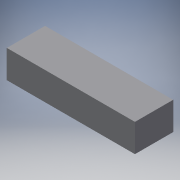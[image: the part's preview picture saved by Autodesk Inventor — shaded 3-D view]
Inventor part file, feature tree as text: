
AUTODESK INVENTOR PART (.ipt)
format: ipt  version: 2016 (Build 200138000, 138)  size: 91,648 bytes
history: native  units: mm
features: other x1, extrude x1, sketch x1
ambient origin geometry x8: Origin, YZ Plane, XZ Plane, XY Plane, X Axis, Y Axis, Z Axis, Center Point
bodies: Solid1 (feature_tree)
feature tree (3):
  parser-record x1  (decoder bookkeeping rows leaked as tree rows — omitted from the tree; the rows remain in map.json)
  extrude  "Extrusion1"  [1 undecoded]
  sketch  "Sketch1"  dims[d3=0.0mm]
note: 1 required parameter value undecoded (feature->parameter linkage not recoverable at this tier; creation-order binding heuristic only, values carry confidence <= 0.55)
note: 1 file-system path scrubbed to <path> (originals preserved in map.json)
